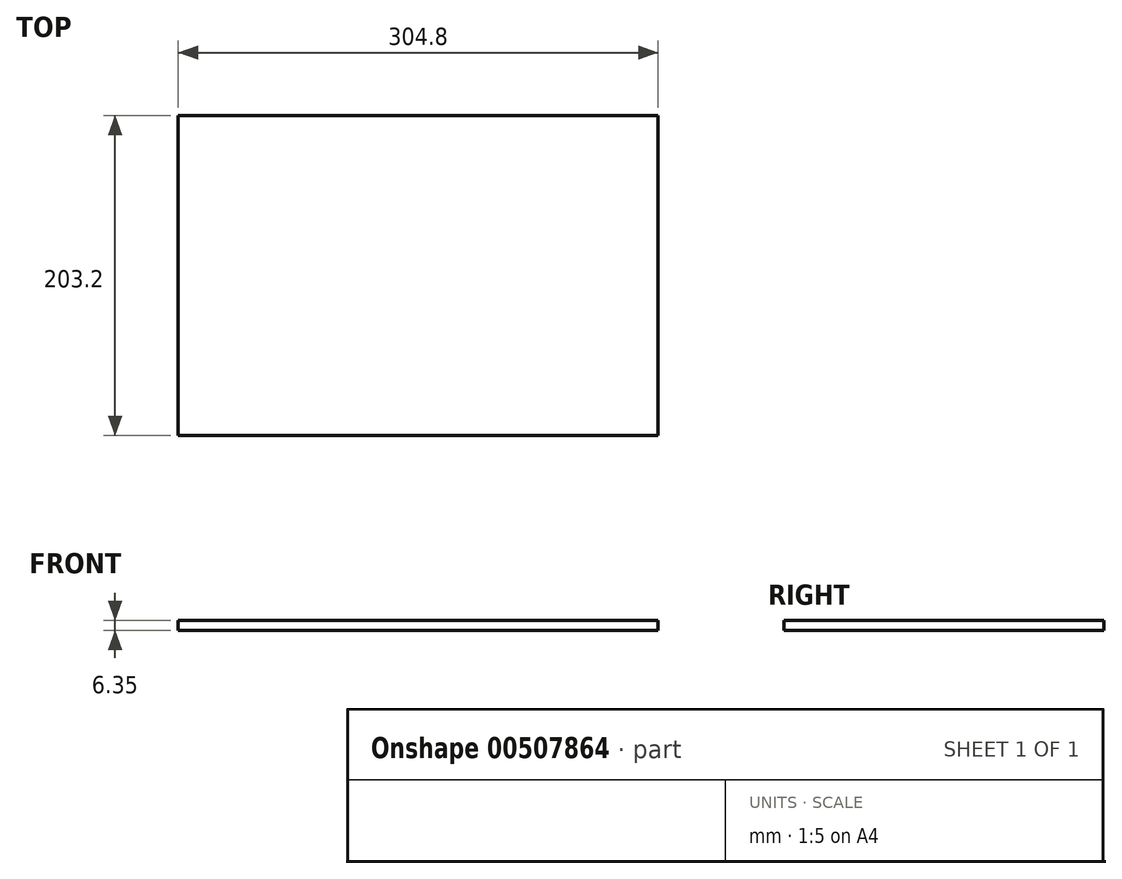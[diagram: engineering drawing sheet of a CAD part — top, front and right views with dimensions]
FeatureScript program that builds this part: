
annotation { "Feature Type Name" : "Feature", "Feature Type Description" : "" }
export const myFeature = defineFeature(function(context is Context, id is Id, definition is map)
    precondition{}
    {
        {
            var Q0;
            Q0=qCreatedBy(makeId("Top.planeOp"),FACE);
            var sketch = newSketch(context, id + "F0", { "sketchPlane" : qUnion([Q0])});
            skLineSegment(sketch, "E0.bottom", {"start": v(-152.4, 101.6) * mm, "end": v(152.4, 101.6) * mm});
            skLineSegment(sketch, "E0.top", {"start": v(-152.4, -101.6) * mm, "end": v(152.4, -101.6) * mm});
            skLineSegment(sketch, "E0.left", {"start": v(-152.4, 101.6) * mm, "end": v(-152.4, -101.6) * mm});
            skLineSegment(sketch, "E0.right", {"start": v(152.4, 101.6) * mm, "end": v(152.4, -101.6) * mm});
            skPoint(sketch, "E0.middle", {"position": v(0, 0) * mm});
            skSolve(sketch);
        }
        {
            var Q0;
            Q0 = qSketchRegion(id + "F0", true);
            extrude(context, id + "F1", {"entities" : qUnion([Q0]), "depth" : 6.35 * mm});
        }
    });
